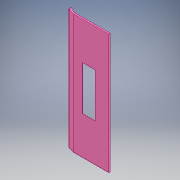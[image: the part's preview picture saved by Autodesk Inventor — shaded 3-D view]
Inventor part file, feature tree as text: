
AUTODESK INVENTOR PART (.ipt)
format: ipt  version: 2018 (Build 220112000, 112)  size: 163,328 bytes
history: native  units: mm
features: extrude x5, sketch x5, projected_geometry x1
ambient origin geometry x8: Origin, YZ Plane, XZ Plane, XY Plane, X Axis, Y Axis, Z Axis, Center Point
bodies: Solid1 (feature_tree)
feature tree (11):
  extrude  "Extrusion1"  Depth=560.0mm
  extrude  "Extrusion2"  Depth=1900.0mm TaperAngle=0.0deg
  extrude  "Extrusion3"  Depth=1.6mm
  extrude  "Extrusion4"  Depth=1.6mm TaperAngle=0.0deg
  extrude  "Extrusion5"  Depth=1.6mm
  sketch  "Sketch1"  dims[d0=560.0mm d2=100.0mm]
  sketch  "Sketch2"  dims[d3=37.0mm d5=1900.0mm d6=0.0mm]
  sketch  "Sketch3"  dims[d9=30.0mm d10=1.6mm]
  projected_geometry  "Projected Loop1"
  sketch  "Sketch4"  dims[d11=20.0mm d12=1.6mm d13=0.0mm]
  sketch  "Sketch5"  dims[d14=1.6mm d15=0.0mm d16=1.6mm d17=20.0mm d18=1.6mm d19=20.0mm d20=1160.0mm d21=0.0mm d22=200.0mm d23=700.0mm d24=600.0mm d25=10.0mm d26=0.0mm]
